# Revit family: 1323xxx Digit II LED - Configuration - Closed
name_source: partatom
category: Lighting Fixtures
units: mm (PartAtom-declared; Revit-internal decimal feet)

## family parameters
Always vertical = Yes
Cut with Voids When Loaded = No
Host = Wall
Light Source = No
OmniClass Number = 23.80.70.00
OmniClass Title = Lighting
Part Type = Normal
Room Calculation Point = No
Round Connector Dimension = Use Diameter
Shared = No

## types (2) — shared parameters
Driver Required = No
Manufacturer = Astro Lighting Ltd
Manufacturer URL - North America = us.astrolighting.com
URL = www.astrolighting.com
zero-valued in all types: Default Elevation

## per-type parameters (varying)
| type | ADA compliant | Dimmable | Dimming Method | Driver Included | Efficacy (lm/w) | Electrical Class | Lamp | Length of Cable Supplied | Light Source Fixed | Location / IP Rating | Main Finish | Main Material | Manufacturer URL - Europe and Rest of World | Power (Watts) | Product CCT | Product CRI | Product Dimensions (MM) | Product Location | Product Name | Product SKU | Product Weight (KG) | Wattage Comments |
| CE | N / A | No | Not Applicable | Yes (Integral) | 27.3 | 2 | LED | Not Applicable | Adjustable | Indoor / IP20 | Polished Chrome | Metal - Zinc | https://www.astrolighting.com | 4.8 | 2700K | 90 | 80 x 190 x 54 | Wall | Digit II LED | 1323010 | 0.614 | 0 |
| ETL |  |  |  |  |  | 0 |  |  |  | DAMP |  | Metal - Steel | www.astrolighting.com |  | 2700K / 3000K | 80 / 90 |  | Bathroom |  | 1234001 |  |  |

## geometry (parser evidence)
native form markers: Sweep x3
no freeform markers — native parametric forms only
